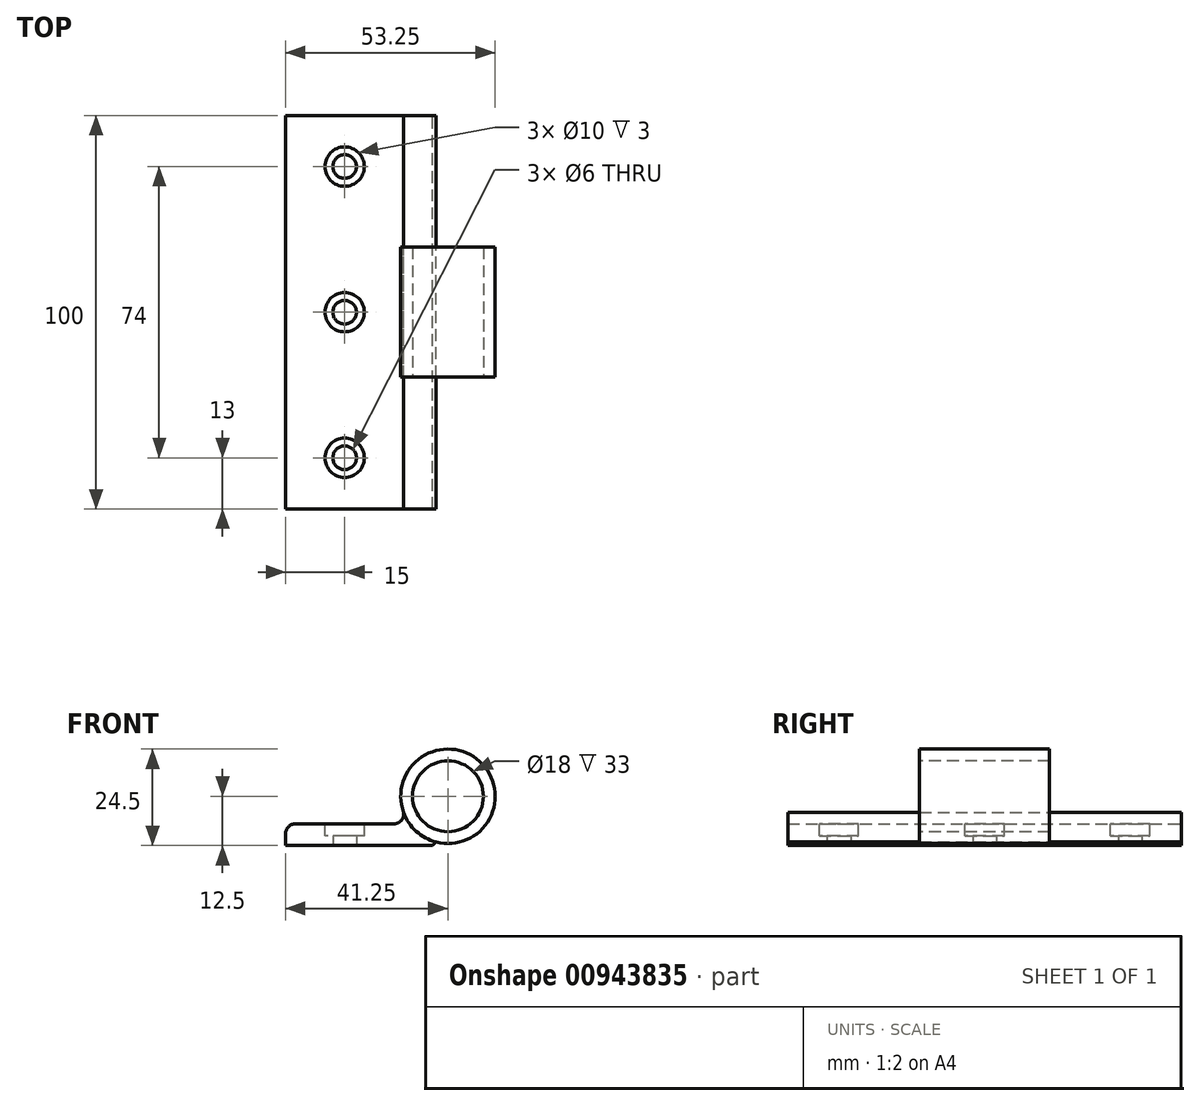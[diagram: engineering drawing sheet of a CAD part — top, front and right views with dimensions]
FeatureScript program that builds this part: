
annotation { "Feature Type Name" : "Feature", "Feature Type Description" : "" }
export const myFeature = defineFeature(function(context is Context, id is Id, definition is map)
    precondition{}
    {
        {
            var Q0;
            Q0=qCreatedBy(makeId("Front.planeOp"),FACE);
            var sketch = newSketch(context, id + "F0", { "sketchPlane" : qUnion([Q0])});
            skLineSegment(sketch, "E0.top", {"start": v(0, 5.5) * mm, "end": v(27.5, 5.5) * mm});
            skLineSegment(sketch, "E0.left", {"start": v(0, 0) * mm, "end": v(0, 5.5) * mm});
            skLineSegment(sketch, "E1", {"start": v(41.25, 12.5) * mm, "end": v(41.25, 0) * mm, "construction": true});
            skCircle(sketch, "E2", {"center": v(41.25, 12.5) * mm, "radius": 12 * mm});
            skLineSegment(sketch, "E3", {"start": v(41.25, 12.5) * mm, "end": v(0, 12.5) * mm, "construction": true});
            skArc(sketch, "E4", {"start": v(27.5, 5.5) * mm, "mid": v(29.41, 6.39) * mm, "end": v(29.96, 8.42) * mm});
            skLineSegment(sketch, "E5", {"start": v(37.37, 0) * mm, "end": v(38.25, 0.88) * mm});
            skLineSegment(sketch, "E6", {"start": v(0, 0) * mm, "end": v(37.37, 0) * mm});
            skSolve(sketch);
        }
        {
            var Q0;
            Q0 = qSketchRegion(id + "F0", true);
            extrude(context, id + "F1", {"entities" : qUnion([Q0]), "depth" : 100 * mm, "offsetDistance" : 25 * mm, "symmetric" : true});
        }
        {
            var Q0;
            Q0=makeQuery(id+"F1.opExtrude","SWEPT_EDGE",EDGE,{"disambiguationData":[OSD([sQuery(id+"F0.wireOp",EDGE,"E0.top"),sQuery(id+"F0.wireOp",EDGE,"E0.left")])]});
            fillet(context, id + "F2", {"entities" : qUnion([Q0]), "radius" : 2.5 * mm, "tangentPropagation" : true, "allowEdgeOverflow" : false});
        }
        {
            var Q0;
            Q0=makeQuery(id+"F1.opExtrude","CAP_FACE",FACE,{"disambiguationData":[OSD([sQuery(id+"F0.wireOp",EDGE,"E0.top"),sQuery(id+"F0.wireOp",EDGE,"E0.left"),sQuery(id+"F0.wireOp",EDGE,"E2"),sQuery(id+"F0.wireOp",EDGE,"E4"),sQuery(id+"F0.wireOp",EDGE,"E5"),sQuery(id+"F0.wireOp",EDGE,"E6")])],"isStart":false});
            var sketch = newSketch(context, id + "F3", { "sketchPlane" : qUnion([Q0])});
            skCircle(sketch, "E7", {"center": v(41.25, 12.5) * mm, "radius": 9 * mm});
            skSolve(sketch);
        }
        {
            var Q0;
            Q0 = qSketchRegion(id + "F3", true);
            extrude(context, id + "F4", {"entities" : qUnion([Q0]), "operationType" : NewBodyOperationType.REMOVE, "endBound" : BoundingType.UP_TO_NEXT, "oppositeDirection" : true, "depth" : 25 * mm, "offsetDistance" : 25 * mm});
        }
        {
            var Q0;
            Q0=makeQuery(id+"F1.opExtrude","CAP_FACE",FACE,{"disambiguationData":[OSD([sQuery(id+"F0.wireOp",EDGE,"E0.top"),sQuery(id+"F0.wireOp",EDGE,"E0.left"),sQuery(id+"F0.wireOp",EDGE,"E2"),sQuery(id+"F0.wireOp",EDGE,"E4"),sQuery(id+"F0.wireOp",EDGE,"E5"),sQuery(id+"F0.wireOp",EDGE,"E6")])],"isStart":false});
            var sketch = newSketch(context, id + "F5", { "sketchPlane" : qUnion([Q0])});
            skCircle(sketch, "E8", {"center": v(41.25, 12.5) * mm, "radius": 12 * mm});
            skSolve(sketch);
        }
        {
            var Q0;
            Q0=makeQuery(id+"F1.opExtrude","CAP_FACE",FACE,{"disambiguationData":[OSD([sQuery(id+"F0.wireOp",EDGE,"E0.top"),sQuery(id+"F0.wireOp",EDGE,"E0.left"),sQuery(id+"F0.wireOp",EDGE,"E2"),sQuery(id+"F0.wireOp",EDGE,"E4"),sQuery(id+"F0.wireOp",EDGE,"E5"),sQuery(id+"F0.wireOp",EDGE,"E6")])],"isStart":true});
            var sketch = newSketch(context, id + "F6", { "sketchPlane" : qUnion([Q0])});
            skCircle(sketch, "E9", {"center": v(-41.25, 12.5) * mm, "radius": 12 * mm});
            skSolve(sketch);
        }
        {
            var Q0;
            Q0 = qSketchRegion(id + "F5", true);
            extrude(context, id + "F7", {"entities" : qUnion([Q0]), "operationType" : NewBodyOperationType.REMOVE, "oppositeDirection" : true, "depth" : 33.5 * mm, "offsetDistance" : 25 * mm});
        }
        {
            var Q0;
            Q0 = qSketchRegion(id + "F6", true);
            extrude(context, id + "F8", {"entities" : qUnion([Q0]), "operationType" : NewBodyOperationType.REMOVE, "oppositeDirection" : true, "depth" : 33.5 * mm, "offsetDistance" : 25 * mm});
        }
        {
            var Q0;
            Q0=makeQuery(id+"F1.opExtrude","SWEPT_FACE",FACE,{"disambiguationData":[OSD([sQuery(id+"F0.wireOp",EDGE,"E0.top")])]});
            var sketch = newSketch(context, id + "F9", { "sketchPlane" : qUnion([Q0])});
            skLineSegment(sketch, "E10", {"start": v(15, 50) * mm, "end": v(15, -50) * mm, "construction": true});
            skCircle(sketch, "E11", {"center": v(15, 0) * mm, "radius": 5 * mm});
            skCircle(sketch, "E12", {"center": v(15, 37) * mm, "radius": 5 * mm});
            skCircle(sketch, "E13", {"center": v(15, -37) * mm, "radius": 5 * mm});
            skSolve(sketch);
        }
        {
            var Q0;
            Q0=makeQuery(id+"F1.opExtrude","SWEPT_FACE",FACE,{"disambiguationData":[OSD([sQuery(id+"F0.wireOp",EDGE,"E6")])]});
            var sketch = newSketch(context, id + "F10", { "sketchPlane" : qUnion([Q0])});
            skCircle(sketch, "E14", {"center": v(15, -37) * mm, "radius": 3 * mm});
            skCircle(sketch, "E15", {"center": v(15, 0) * mm, "radius": 3 * mm});
            skCircle(sketch, "E16", {"center": v(15, 37) * mm, "radius": 3 * mm});
            skSolve(sketch);
        }
        {
            var Q0;
            Q0 = qSketchRegion(id + "F9", true);
            extrude(context, id + "F11", {"entities" : qUnion([Q0]), "operationType" : NewBodyOperationType.REMOVE, "oppositeDirection" : true, "depth" : 3 * mm, "offsetDistance" : 25 * mm});
        }
        {
            var Q0;
            Q0 = qSketchRegion(id + "F10", true);
            extrude(context, id + "F12", {"entities" : qUnion([Q0]), "operationType" : NewBodyOperationType.REMOVE, "endBound" : BoundingType.UP_TO_NEXT, "oppositeDirection" : true, "depth" : 25 * mm, "offsetDistance" : 25 * mm});
        }
    });
